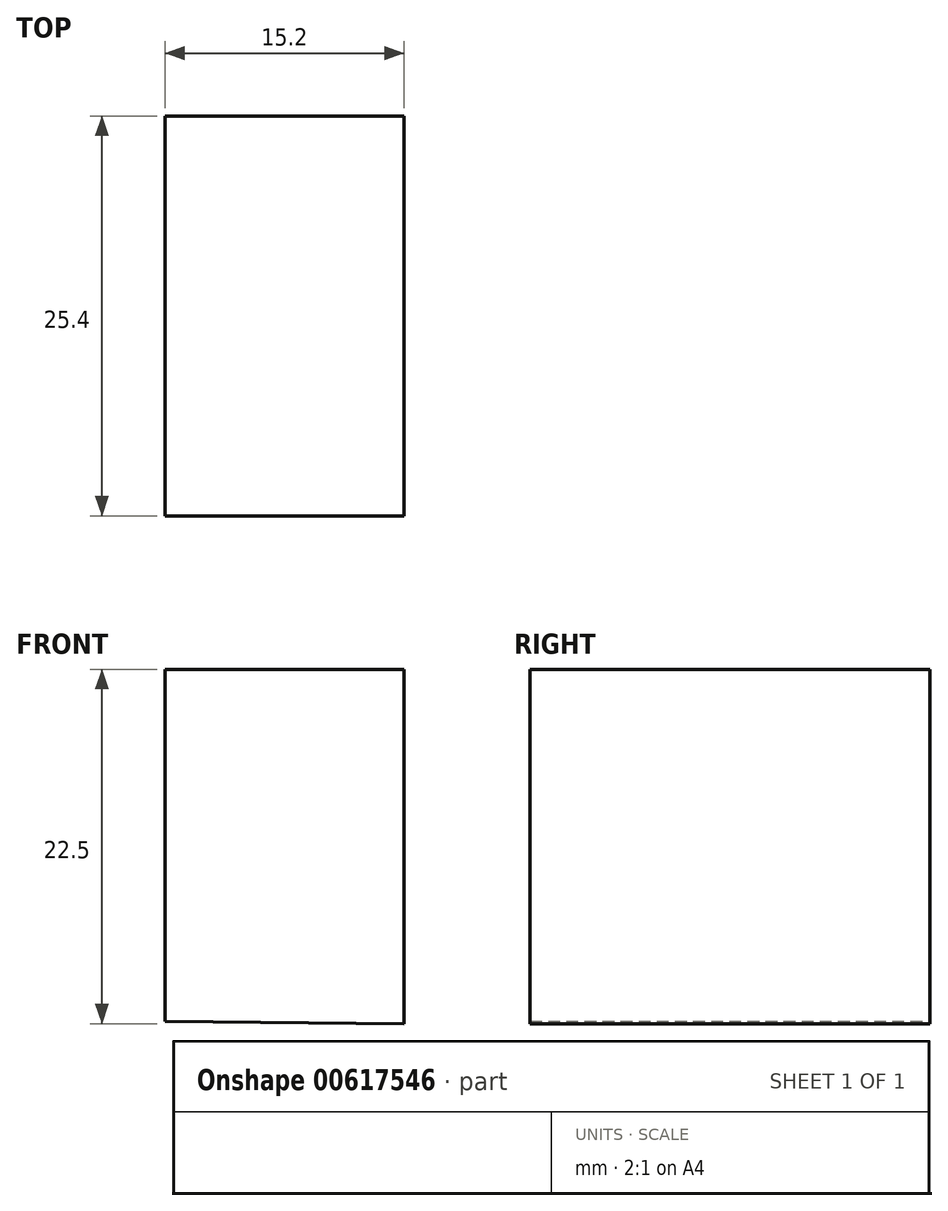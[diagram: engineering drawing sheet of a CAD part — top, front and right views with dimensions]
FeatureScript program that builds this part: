
annotation { "Feature Type Name" : "Feature", "Feature Type Description" : "" }
export const myFeature = defineFeature(function(context is Context, id is Id, definition is map)
    precondition{}
    {
        {
            var Q0;
            Q0=qCreatedBy(makeId("Front.planeOp"),FACE);
            var sketch = newSketch(context, id + "F0", { "sketchPlane" : qUnion([Q0])});
            skLineSegment(sketch, "E0", {"start": v(-8.63, 5.92) * mm, "end": v(6.57, 5.92) * mm});
            skLineSegment(sketch, "E1", {"start": v(6.57, 5.92) * mm, "end": v(6.57, -16.58) * mm});
            skLineSegment(sketch, "E2", {"start": v(-8.63, 5.92) * mm, "end": v(-8.63, -16.44) * mm});
            skLineSegment(sketch, "E3", {"start": v(-8.63, -16.44) * mm, "end": v(6.57, -16.58) * mm});
            skSolve(sketch);
        }
        {
            var Q0;
            Q0 = qSketchRegion(id + "F0", true);
            extrude(context, id + "F1", {"entities" : qUnion([Q0]), "depth" : 25.4 * mm, "offsetDistance" : 25.4 * mm});
        }
    });
